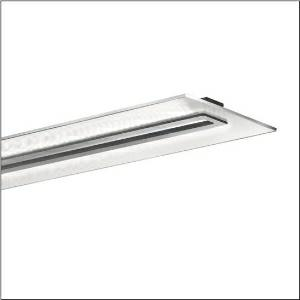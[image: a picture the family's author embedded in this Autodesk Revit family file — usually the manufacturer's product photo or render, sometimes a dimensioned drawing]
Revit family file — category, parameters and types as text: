
# Revit family: vega_r__11_5mn238dlc003_c003
name_source: partatom
category: Lighting Fixtures
units: mm (PartAtom-declared; Revit-internal decimal feet)

## family parameters
Cut with Voids When Loaded = No
Host = Face
Light Source = No
Part Type = Normal
Room Calculation Point = No
Round Connector Dimension = Use Diameter
Shared = No

## types (1)
- --- (1 x LED 3000K / CRI = 80 (unbekannt), 4300 lm, 3000K)
    Apparent Load = 35 VA
    CIE Flux Codes = 61 86 97 62 100
    Color Rendering = 80
    Color Temperature = 3000K
    Default Elevation = 1800 mm
    Description = Vega® 11, office luminaire, primary light control with prismatic reflector, of PMMA, transparent prismatic structure, CAT 2 (L<= 1500cd/m²), light emission: direct/indirect distribution, primary light characteristic: symmetric, installation type: suspended mounting, surface-mounted, LED, rated luminous flux: 4.300lm, luminous efficacy: 123lm/W, light colour: 830, colour temperature: 3000K, control gear: DALI, with terminal, 3+2-pole, max. 2.5mm², mains connection: 230V, AC, 50Hz, connection cable inclusive, cable length: 1,5m, rated input power: 35W, luminaire housing, rectangular, rounded, of aluminium section, anodised, metallic grey (RAL 9006), length: 1.250mm, width: 350mm, height: 43mm, luminaire housing, lower part, of aluminium section, anodised, metallic grey (RAL 9006), of PC, grey, protection rating (complete): IP20, insulation class (complete): insulation class I (protective earthing), certification: CE, standard: EN 50419, packaging unit: 1 piece
    Height = 40 mm  [stored 0.131234 ft]
    Lamp = 1 x LED 3000K / CRI >= 80 (unbekannt)
    Lamp Light Flux = 4300 lm
    Lamp count = 1
    Length = 1250 mm
    Luminous efficacy = 123 lm/W
    Manufacturer = Siteco
    ModVariant = No
    Model = 5MN238DLC003
    Mounting Place = Ceiling
    Mounting Type = Pendant
    Number of Poles = 1
    OnlyDefault = Yes
    Power Factor = 1
    Product Name = Vega® 11
    Product group = office luminaire | ceiling pendant
    ProductGroupID = 903
    Protection Class = Protection class I
    Protection Degree = IP 20
    RLX_Detail_Level = 1
    RLX_Emergency_Light_Flux = 0 lm
    RLX_Emergency_Type = 0
    RLX_Emergency_Type_DB = No
    RlxData = <blob elided: 62749 chars, md5=ba1b4e84>
    Socket = socket
    Standby Power = 0 W
    System Light Flux = 4300 lm
    System Power = 35 W
    Type Comments = factory setting: luminous flux: 100 % | dim-lin: 254 | 260 mA
    Type Image = l_1004807.jpg
    URL = http://relux.com
    VarID = @adj_220881
    Voltage = 0 V
    Weight = 0.00 kg
    Width = 350 mm

note: [stored X ft] marks values corroborated as IEEE doubles in the binary element streams (Revit-internal decimal feet)

## geometry (parser evidence)
native form markers: Blend x4, Sweep x15
no freeform markers — native parametric forms only
